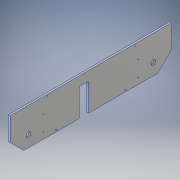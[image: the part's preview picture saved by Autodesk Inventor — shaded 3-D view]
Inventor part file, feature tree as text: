
AUTODESK INVENTOR PART (.ipt)
format: ipt  version: 2019 (Build 230136000, 136)  size: 167,936 bytes
history: native  units: in
note: dims shown in document units (in); Inventor stores cm internally (conversion verified against a paired STEP export)
features: sketch x4, extrude x2, chamfer x2, hole x2, projected_geometry x2
ambient origin geometry x8: Origin, YZ Plane, XZ Plane, XY Plane, X Axis, Y Axis, Z Axis, Center Point
bodies: Solid1 (feature_tree)
feature tree (12):
  extrude  "Extrusion1"  Depth=17.5in
  chamfer  "Chamfer1"  Distance=2.0in
  chamfer  "Chamfer2"  Distance=0.1875in
  hole  "Hole1"  [1 undecoded]
  hole  "Hole2"  [1 undecoded]
  extrude  "Extrusion6"  Depth=3.0in
  sketch  "Sketch1"  dims[d0=4.0in d1=17.5in]
  sketch  "Sketch6"  dims[d2=0.501in]
  projected_geometry  "Projected Loop5"
  sketch  "Sketch7"  dims[d3=1.25in]
  projected_geometry  "Projected Loop6"
  sketch  "Sketch8"  dims[d4=2.0in d5=2.0in d6=0.1875in d7=0.0in d8=1.5in d9=0.125in d10=45.0deg d11=1.5in d12=0.125in d13=45.0deg d22=6.517in d23=0.125in d24=0.603in d25=0.125in d26=0.63in d27=6.517in d28=0.125in d29=0.603in d30=6.517in d31=0.125in d32=0.63in d33=6.517in d80=1.7in d83=0.65in d86=1.7in d88=0.08in d89=0.75in d90=0.375in d91=0.25in d92=0.5635in d93=1.0in d94=0.8108in d95=0.175in d96=0.175in d97=0.175in d98=0.175in d99=4.0in d100=4.0in d101=5.0in d102=5.0in d103=0.15in d104=0.75in d105=0.375in d106=0.25in d107=0.5635in d108=1.0in d109=0.8108in d110=1.0in d111=0.0in d112=1.0in d113=7.5in d114=3.0in d115=3.625in d116=3.625in d117=0.65in d118=3.625in d119=3.625in]
note: 2 required parameter values undecoded (feature->parameter linkage not recoverable at this tier; creation-order binding heuristic only, values carry confidence <= 0.55)
